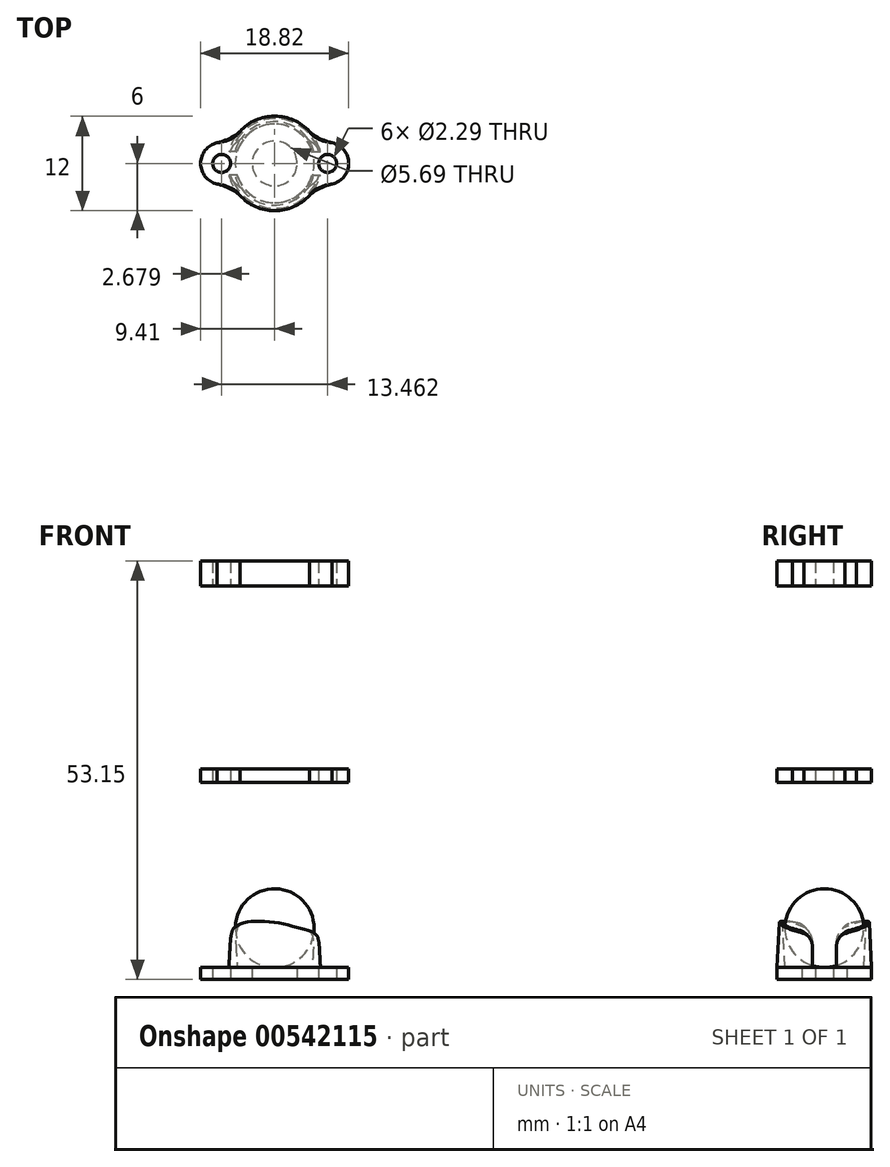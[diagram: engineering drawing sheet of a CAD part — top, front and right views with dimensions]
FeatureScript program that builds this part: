
annotation { "Feature Type Name" : "Feature", "Feature Type Description" : "" }
export const myFeature = defineFeature(function(context is Context, id is Id, definition is map)
    precondition{}
    {
        {
            var Q0;
            Q0=qCreatedBy(makeId("Top.planeOp"),FACE);
            var sketch = newSketch(context, id + "F0", { "sketchPlane" : qUnion([Q0])});
            skCircle(sketch, "E0", {"center": v(-6.73, 0) * mm, "radius": 1.14 * mm});
            skCircle(sketch, "E1", {"center": v(6.73, 0) * mm, "radius": 1.14 * mm});
            skArc(sketch, "E2", {"start": v(-4.43, -4.06) * mm, "mid": v(0, -6) * mm, "end": v(4.43, -4.06) * mm});
            skArc(sketch, "E3", {"start": v(-7.3, 2.62) * mm, "mid": v(-9.4, 0) * mm, "end": v(-7.3, -2.62) * mm});
            skArc(sketch, "E4", {"start": v(7.3, -2.62) * mm, "mid": v(9.4, 0) * mm, "end": v(7.3, 2.62) * mm});
            skCircle(sketch, "E5", {"center": v(0, 0) * mm, "radius": 2.85 * mm});
            skPoint(sketch, "E6", {"position": v(-5.51, 2.38) * mm});
            skArc(sketch, "E7.trimOffspring", {"start": v(4.43, 4.06) * mm, "mid": v(0, 6) * mm, "end": v(-4.43, 4.06) * mm});
            skFitSpline(sketch, "E8", {"points": [v(-7.3, 2.62) * mm, v(-4.43, 4.06) * mm], "startDerivative": vector(3.28, 0.71) * mm, "endDerivative": vector(1.57, 1.72) * mm});
            skFitSpline(sketch, "E9.MirrorCS", {"points": [v(-7.3, -2.62) * mm, v(-4.43, -4.06) * mm], "startDerivative": vector(3.28, -0.71) * mm, "endDerivative": vector(1.57, -1.72) * mm});
            skFitSpline(sketch, "E10.MirrorCS", {"points": [v(7.3, 2.62) * mm, v(4.43, 4.06) * mm], "startDerivative": vector(-3.28, 0.71) * mm, "endDerivative": vector(-1.57, 1.72) * mm});
            skFitSpline(sketch, "E11.MirrorCS", {"points": [v(7.3, -2.62) * mm, v(4.43, -4.06) * mm], "startDerivative": vector(-3.28, -0.71) * mm, "endDerivative": vector(-1.57, -1.72) * mm});
            skSolve(sketch);
        }
        {
            var Q0;
            Q0=qSketchRegion(id+"F0",true);
            extrude(context, id + "F1", {"entities" : qUnion([Q0]), "depth" : 1.5 * mm});
        }
        {
            var Q0;
            Q0=makeQuery(id+"F1.opExtrude","CAP_FACE",FACE,{"disambiguationData":[OSD([sQuery(id+"F0.wireOp",EDGE,"E0"),sQuery(id+"F0.wireOp",EDGE,"E1"),sQuery(id+"F0.wireOp",EDGE,"E2"),sQuery(id+"F0.wireOp",EDGE,"E3"),sQuery(id+"F0.wireOp",EDGE,"E4"),sQuery(id+"F0.wireOp",EDGE,"E5"),sQuery(id+"F0.wireOp",EDGE,"E7.trimOffspring"),sQuery(id+"F0.wireOp",EDGE,"E8"),sQuery(id+"F0.wireOp",EDGE,"E9.MirrorCS"),sQuery(id+"F0.wireOp",EDGE,"E10.MirrorCS"),sQuery(id+"F0.wireOp",EDGE,"E11.MirrorCS")])],"isStart":false});
            var sketch = newSketch(context, id + "F2", { "sketchPlane" : qUnion([Q0])});
            skCircle(sketch, "E12", {"center": v(0, 0) * mm, "radius": 6 * mm});
            skCircle(sketch, "E13.0", {"center": v(0, 0) * mm, "radius": 5 * mm});
            skSolve(sketch);
        }
        {
            var Q0;
            Q0=makeQuery(id+"F2.imprint","IMPRINT",FACE,{"disambiguationData":[TD([[makeQuery(id+"F2.imprint","IMPRINT",EDGE,{"derivedFrom":sQuery(id+"F2.wireOp",EDGE,"E13.0")}),-1.0]])]});
            extrude(context, id + "F3", {"entities" : qUnion([Q0]), "operationType" : NewBodyOperationType.ADD, "depth" : 5.9 * mm, "hasDraft" : true, "draftAngle" : 3 * degree, "draftPullDirection" : true});
        }
        {
            var Q0;
            Q0=qCreatedBy(makeId("Front.planeOp"),FACE);
            var sketch = newSketch(context, id + "F4", { "sketchPlane" : qUnion([Q0])});
            skFitSpline(sketch, "E14", {"points": [v(-5.95, 1.5) * mm, v(-5.77, 4.78) * mm, v(-5.4, 6.25) * mm, v(-4.4, 7.04) * mm, v(-2.83, 7.35) * mm, v(-0.78, 7.32) * mm, v(0.86, 7.09) * mm, v(3.12, 6.53) * mm, v(3.88, 6.33) * mm, v(4.8, 6.01) * mm, v(5.18, 5.77) * mm, v(5.46, 5.4) * mm, v(5.74, 4.49) * mm, v(5.95, 1.5) * mm], "startDerivative": vector(0, 30.3) * mm, "endDerivative": vector(1.07, -30.08) * mm});
            skLineSegment(sketch, "E15", {"start": v(-5.95, 1.5) * mm, "end": v(5.95, 1.5) * mm});
            skLineSegment(sketch, "E16", {"start": v(-5.95, 1.5) * mm, "end": v(-9.53, 1.5) * mm});
            skLineSegment(sketch, "E17", {"start": v(-9.53, 1.5) * mm, "end": v(-9.53, 0) * mm});
            skLineSegment(sketch, "E18", {"start": v(-9.53, 0) * mm, "end": v(9.53, 0) * mm});
            skLineSegment(sketch, "E19", {"start": v(9.53, 0) * mm, "end": v(9.53, 1.5) * mm});
            skLineSegment(sketch, "E20", {"start": v(9.53, 1.5) * mm, "end": v(5.95, 1.5) * mm});
            skSolve(sketch);
        }
        {
            var Q0;
            Q0=qSketchRegion(id+"F4",true);
            extrude(context, id + "F5", {"entities" : qUnion([Q0]), "operationType" : NewBodyOperationType.INTERSECT, "endBound" : BoundingType.SYMMETRIC, "depth" : 25 * mm});
        }
        {
            var Q0;
            Q0=qCreatedBy(makeId("Right.planeOp"),FACE);
            var Q1;
            {var subQ0=sQuery(id+"F2.wireOp",EDGE,"E12");var subQ1=sQuery(id+"F0.wireOp",EDGE,"E0");Q1=makeQuery(id+"F3.opExtrude","CAP_VERTEX",VERTEX,{"disambiguationData":[OSD([subQ1,subQ0]),TDD([makeQuery(id+"F2.imprint","INTERSECT",VERTEX,{"disambiguationData":[OD(0.0)],"derivedFrom":[makeQuery(id+"F1.opExtrude","CAP_EDGE",EDGE,{"disambiguationData":[OSD([subQ1])],"isStart":false}),subQ0]})])],"isStart":true});}
            cPlane(context, id + "F6", {"entities" : qUnion([Q0, Q1]), "cplaneType" : CPlaneType.PLANE_POINT, "offset" : 25 * mm, "width" : 150 * mm, "height" : 150 * mm});
        }
        {
            var Q0;
            Q0=qCreatedBy(id+"F6.planeOp",FACE);
            var sketch = newSketch(context, id + "F7", { "sketchPlane" : qUnion([Q0])});
            skLineSegment(sketch, "E21.bottom", {"start": v(1.5, 1.5) * mm, "end": v(-1.5, 1.5) * mm});
            skLineSegment(sketch, "E21.left", {"start": v(1.5, 1.5) * mm, "end": v(1.5, 4.42) * mm});
            skLineSegment(sketch, "E21.right", {"start": v(-1.5, 1.5) * mm, "end": v(-1.5, 4.42) * mm});
            skLineSegment(sketch, "E22", {"start": v(-4.5, 7.42) * mm, "end": v(-6.48, 7.42) * mm});
            skLineSegment(sketch, "E23", {"start": v(-6.48, 7.42) * mm, "end": v(-6.48, 8.72) * mm});
            skLineSegment(sketch, "E24", {"start": v(6.48, 8.72) * mm, "end": v(6.48, 7.42) * mm});
            skLineSegment(sketch, "E25", {"start": v(6.48, 7.42) * mm, "end": v(4.5, 7.42) * mm});
            skPoint(sketch, "E26.newPointB", {"position": v(-4.16, 7.42) * mm});
            skArc(sketch, "E26.filletArc", {"start": v(-1.5, 4.42) * mm, "mid": v(-2.38, 6.55) * mm, "end": v(-4.5, 7.42) * mm});
            skPoint(sketch, "E27.newPointA", {"position": v(-1.16, 7.42) * mm});
            skArc(sketch, "E27.filletArc", {"start": v(4.5, 7.42) * mm, "mid": v(2.38, 6.55) * mm, "end": v(1.5, 4.42) * mm});
            skLineSegment(sketch, "E28", {"start": v(6.48, 8.72) * mm, "end": v(-6.48, 8.72) * mm});
            skSolve(sketch);
        }
        {
            var Q0;
            Q0=makeQuery(id+"F7.imprint","IMPRINT",FACE,{"disambiguationData":[TD([[makeQuery(id+"F7.imprint","IMPRINT",EDGE,{"derivedFrom":sQuery(id+"F7.wireOp",EDGE,"E21.bottom")}),-1.0]])]});
            extrude(context, id + "F8", {"entities" : qUnion([Q0]), "operationType" : NewBodyOperationType.REMOVE, "depth" : 5 * mm});
        }
        {
            var Q0;
            Q0=qCreatedBy(makeId("Right.planeOp"),FACE);
            var Q1;
            {var subQ0=sQuery(id+"F2.wireOp",EDGE,"E12");var subQ1=sQuery(id+"F0.wireOp",EDGE,"E1");Q1=makeQuery(id+"F3.opExtrude","CAP_VERTEX",VERTEX,{"disambiguationData":[OSD([subQ1,subQ0]),TDD([makeQuery(id+"F2.imprint","INTERSECT",VERTEX,{"disambiguationData":[OD(1.0)],"derivedFrom":[makeQuery(id+"F1.opExtrude","CAP_EDGE",EDGE,{"disambiguationData":[OSD([subQ1])],"isStart":false}),subQ0]})])],"isStart":true});}
            cPlane(context, id + "F9", {"entities" : qUnion([Q0, Q1]), "cplaneType" : CPlaneType.PLANE_POINT, "offset" : 25 * mm, "width" : 150 * mm, "height" : 150 * mm});
        }
        {
            var Q0;
            Q0=qCreatedBy(id+"F9.planeOp",FACE);
            var sketch = newSketch(context, id + "F10", { "sketchPlane" : qUnion([Q0])});
            skLineSegment(sketch, "E29", {"start": v(-1.5, 1.5) * mm, "end": v(-1.5, 3.98) * mm});
            skLineSegment(sketch, "E30.bottom", {"start": v(-1.5, 1.5) * mm, "end": v(0, 1.5) * mm});
            skLineSegment(sketch, "E30.left", {"start": v(-1.5, 1.5) * mm, "end": v(-1.5, 1.5) * mm});
            skLineSegment(sketch, "E30.right", {"start": v(0, 1.5) * mm, "end": v(0, 1.5) * mm});
            skArc(sketch, "E31", {"start": v(-1.5, 3.98) * mm, "mid": v(-1.97, 5.4) * mm, "end": v(-3.18, 6.25) * mm});
            skLineSegment(sketch, "E32", {"start": v(-3.18, 6.25) * mm, "end": v(-3.18, 6.91) * mm});
            skLineSegment(sketch, "E33", {"start": v(-3.18, 6.91) * mm, "end": v(0, 6.91) * mm});
            skLineSegment(sketch, "E34.MirrorCS", {"start": v(3.18, 6.91) * mm, "end": v(0, 6.91) * mm});
            skLineSegment(sketch, "E35.MirrorCS", {"start": v(3.18, 6.25) * mm, "end": v(3.18, 6.91) * mm});
            skArc(sketch, "E36.MirrorCS", {"start": v(1.5, 3.98) * mm, "mid": v(1.97, 5.4) * mm, "end": v(3.18, 6.25) * mm});
            skLineSegment(sketch, "E37.MirrorCS", {"start": v(1.5, 1.5) * mm, "end": v(1.5, 3.98) * mm});
            skLineSegment(sketch, "E38.MirrorCS", {"start": v(1.5, 1.5) * mm, "end": v(0, 1.5) * mm});
            skSolve(sketch);
        }
        {
            var Q0;
            Q0=qSketchRegion(id+"F10",true);
            extrude(context, id + "F11", {"entities" : qUnion([Q0]), "operationType" : NewBodyOperationType.REMOVE, "oppositeDirection" : true, "depth" : 3 * mm});
        }
        {
            var Q0;
            {var subQ0=sQuery(id+"F0.wireOp",EDGE,"E7.trimOffspring");var subQ2=sQuery(id+"F0.wireOp",EDGE,"E0");var subQ3=sQuery(id+"F0.wireOp",EDGE,"E3");var subQ4=sQuery(id+"F0.wireOp",EDGE,"E2");var subQ6=sQuery(id+"F0.wireOp",EDGE,"E8");var subQ7=sQuery(id+"F0.wireOp",EDGE,"E9.MirrorCS");var subQ11=sQuery(id+"F0.wireOp",EDGE,"E10.MirrorCS");var subQ13=sQuery(id+"F0.wireOp",EDGE,"E1");var subQ16=sQuery(id+"F0.wireOp",EDGE,"E11.MirrorCS");var subQ20=sQuery(id+"F0.wireOp",EDGE,"E5");var subQ21=sQuery(id+"F0.wireOp",EDGE,"E4");var subQ22=makeQuery(id+"F1.opExtrude","CAP_FACE",FACE,{"disambiguationData":[OSD([subQ2,subQ13,subQ4,subQ3,subQ21,subQ20,subQ0,subQ6,subQ7,subQ11,subQ16])],"isStart":false});Q0=makeQuery(id+"F11.boolean.opBoolean","MERGE",FACE,{"derivedFrom":[makeQuery(id+"F3.boolean.opBoolean","SPLIT",FACE,{"disambiguationData":[TD([makeQuery(id+"F1.opExtrude","SWEPT_FACE",FACE,{"disambiguationData":[OSD([subQ13])]})])],"derivedFrom":subQ22}),makeQuery(id+"F8.boolean.opBoolean","MERGE",FACE,{"derivedFrom":[makeQuery(id+"F3.boolean.opBoolean","SPLIT",FACE,{"disambiguationData":[TD([makeQuery(id+"F1.opExtrude","SWEPT_FACE",FACE,{"disambiguationData":[OSD([subQ20])]})])],"derivedFrom":subQ22}),makeQuery(id+"F3.boolean.opBoolean","SPLIT",FACE,{"disambiguationData":[TD([makeQuery(id+"F1.opExtrude","SWEPT_FACE",FACE,{"disambiguationData":[OSD([subQ2])]})])],"derivedFrom":subQ22}),makeQuery(id+"F8.opExtrude","SWEPT_FACE",FACE,{"disambiguationData":[OSD([sQuery(id+"F7.wireOp",EDGE,"E21.bottom")])]})]}),makeQuery(id+"F11.opExtrude","SWEPT_FACE",FACE,{"disambiguationData":[OSD([sQuery(id+"F10.wireOp",EDGE,"E30.bottom"),sQuery(id+"F10.wireOp",EDGE,"E38.MirrorCS")])]})]});}
            cPlane(context, id + "F12", {"entities" : qUnion([Q0]), "cplaneType" : CPlaneType.OFFSET, "offset" : 5 * mm, "width" : 150 * mm, "height" : 150 * mm});
        }
        {
            var Q0;
            Q0=qCreatedBy(id+"F12.planeOp",FACE);
            var sketch = newSketch(context, id + "F13", { "sketchPlane" : qUnion([Q0])});
            skArc(sketch, "E39", {"start": v(0, 5) * mm, "mid": v(-5, 0) * mm, "end": v(0, -5) * mm});
            skLineSegment(sketch, "E40", {"start": v(0, -5) * mm, "end": v(0, 5) * mm, "construction": true});
            skLineSegment(sketch, "E41", {"start": v(0, -5) * mm, "end": v(0, 5) * mm});
            skSolve(sketch);
        }
        {
            var Q0;
            Q0=makeQuery(id+"F13.imprint","IMPRINT",FACE,{"disambiguationData":[TD([[makeQuery(id+"F13.imprint","IMPRINT",EDGE,{"derivedFrom":sQuery(id+"F13.wireOp",EDGE,"E39")}),1.0]])]});
            var Q1;
            Q1=sQuery(id+"F13.wireOp",EDGE,"E40");
            revolve(context, id + "F14", {"entities" : qUnion([Q0]), "axis" : qUnion([Q1]), "revolveType" : RevolveType.FULL});
        }
        {
            var Q0;
            Q0=qCreatedBy(makeId("Top.planeOp"),FACE);
            cPlane(context, id + "F15", {"entities" : qUnion([Q0]), "cplaneType" : CPlaneType.OFFSET, "offset" : 25 * mm, "width" : 150 * mm, "height" : 150 * mm});
        }
        {
            var Q0;
            Q0=qCreatedBy(id+"F15.planeOp",FACE);
            var sketch = newSketch(context, id + "F16", { "sketchPlane" : qUnion([Q0])});
            skFitSpline(sketch, "E42.0.0", {"points": [v(4.43, 4.06) * mm, v(4.95, 3.48) * mm, v(6.2, 2.85) * mm, v(7.3, 2.62) * mm]});
            skArc(sketch, "E42.0.1", {"start": v(7.3, 2.62) * mm, "mid": v(9.4, 0) * mm, "end": v(7.3, -2.62) * mm});
            skFitSpline(sketch, "E42.0.2", {"points": [v(7.3, -2.62) * mm, v(6.2, -2.85) * mm, v(4.95, -3.48) * mm, v(4.43, -4.06) * mm]});
            skArc(sketch, "E42.0.3", {"start": v(4.43, -4.06) * mm, "mid": v(0, -6) * mm, "end": v(-4.43, -4.06) * mm});
            skFitSpline(sketch, "E42.0.4", {"points": [v(-4.43, -4.06) * mm, v(-4.95, -3.48) * mm, v(-6.2, -2.85) * mm, v(-7.3, -2.62) * mm]});
            skArc(sketch, "E42.0.5", {"start": v(-7.3, -2.62) * mm, "mid": v(-9.4, 0) * mm, "end": v(-7.3, 2.62) * mm});
            skFitSpline(sketch, "E42.0.6", {"points": [v(-7.3, 2.62) * mm, v(-6.2, 2.85) * mm, v(-4.95, 3.48) * mm, v(-4.43, 4.06) * mm]});
            skArc(sketch, "E42.0.7", {"start": v(-4.43, 4.06) * mm, "mid": v(0, 6) * mm, "end": v(4.43, 4.06) * mm});
            skCircle(sketch, "E43.0", {"center": v(-6.73, 0) * mm, "radius": 1.14 * mm});
            skCircle(sketch, "E44.0", {"center": v(6.73, 0) * mm, "radius": 1.14 * mm});
            skSolve(sketch);
        }
        {
            var Q0;
            Q0=makeQuery(id+"F16.imprint","IMPRINT",FACE,{"disambiguationData":[TD([[makeQuery(id+"F16.imprint","IMPRINT",EDGE,{"derivedFrom":sQuery(id+"F16.wireOp",EDGE,"E42.0.0")}),-1.0]])]});
            extrude(context, id + "F17", {"entities" : qUnion([Q0]), "depth" : 1.7 * mm});
        }
        {
            var Q0;
            Q0=qCreatedBy(makeId("Top.planeOp"),FACE);
            cPlane(context, id + "F18", {"entities" : qUnion([Q0]), "cplaneType" : CPlaneType.OFFSET, "offset" : 50 * mm, "width" : 150 * mm, "height" : 150 * mm});
        }
        {
            var Q0;
            Q0=qCreatedBy(id+"F18.planeOp",FACE);
            var sketch = newSketch(context, id + "F19", { "sketchPlane" : qUnion([Q0])});
            skArc(sketch, "E45.0.0", {"start": v(4.43, 4.06) * mm, "mid": v(0, 6) * mm, "end": v(-4.43, 4.06) * mm});
            skFitSpline(sketch, "E45.0.1", {"points": [v(-4.43, 4.06) * mm, v(-4.95, 3.48) * mm, v(-6.2, 2.85) * mm, v(-7.3, 2.62) * mm]});
            skArc(sketch, "E45.0.2", {"start": v(-7.3, 2.62) * mm, "mid": v(-9.4, 0) * mm, "end": v(-7.3, -2.62) * mm});
            skFitSpline(sketch, "E45.0.3", {"points": [v(-7.3, -2.62) * mm, v(-6.2, -2.85) * mm, v(-4.95, -3.48) * mm, v(-4.43, -4.06) * mm]});
            skArc(sketch, "E45.0.4", {"start": v(-4.43, -4.06) * mm, "mid": v(0, -6) * mm, "end": v(4.43, -4.06) * mm});
            skFitSpline(sketch, "E45.0.5", {"points": [v(4.43, -4.06) * mm, v(4.95, -3.48) * mm, v(6.2, -2.85) * mm, v(7.3, -2.62) * mm]});
            skArc(sketch, "E45.0.6", {"start": v(7.3, -2.62) * mm, "mid": v(9.4, 0) * mm, "end": v(7.3, 2.62) * mm});
            skFitSpline(sketch, "E45.0.7", {"points": [v(7.3, 2.62) * mm, v(6.2, 2.85) * mm, v(4.95, 3.48) * mm, v(4.43, 4.06) * mm]});
            skCircle(sketch, "E46.0", {"center": v(-6.73, 0) * mm, "radius": 1.14 * mm});
            skCircle(sketch, "E47.0", {"center": v(6.73, 0) * mm, "radius": 1.14 * mm});
            skSolve(sketch);
        }
        {
            var Q0;
            Q0=makeQuery(id+"F19.imprint","IMPRINT",FACE,{"disambiguationData":[TD([[makeQuery(id+"F19.imprint","IMPRINT",EDGE,{"derivedFrom":sQuery(id+"F19.wireOp",EDGE,"E45.0.0")}),1.0]])]});
            extrude(context, id + "F20", {"entities" : qUnion([Q0]), "depth" : 3.15 * mm});
        }
    });
